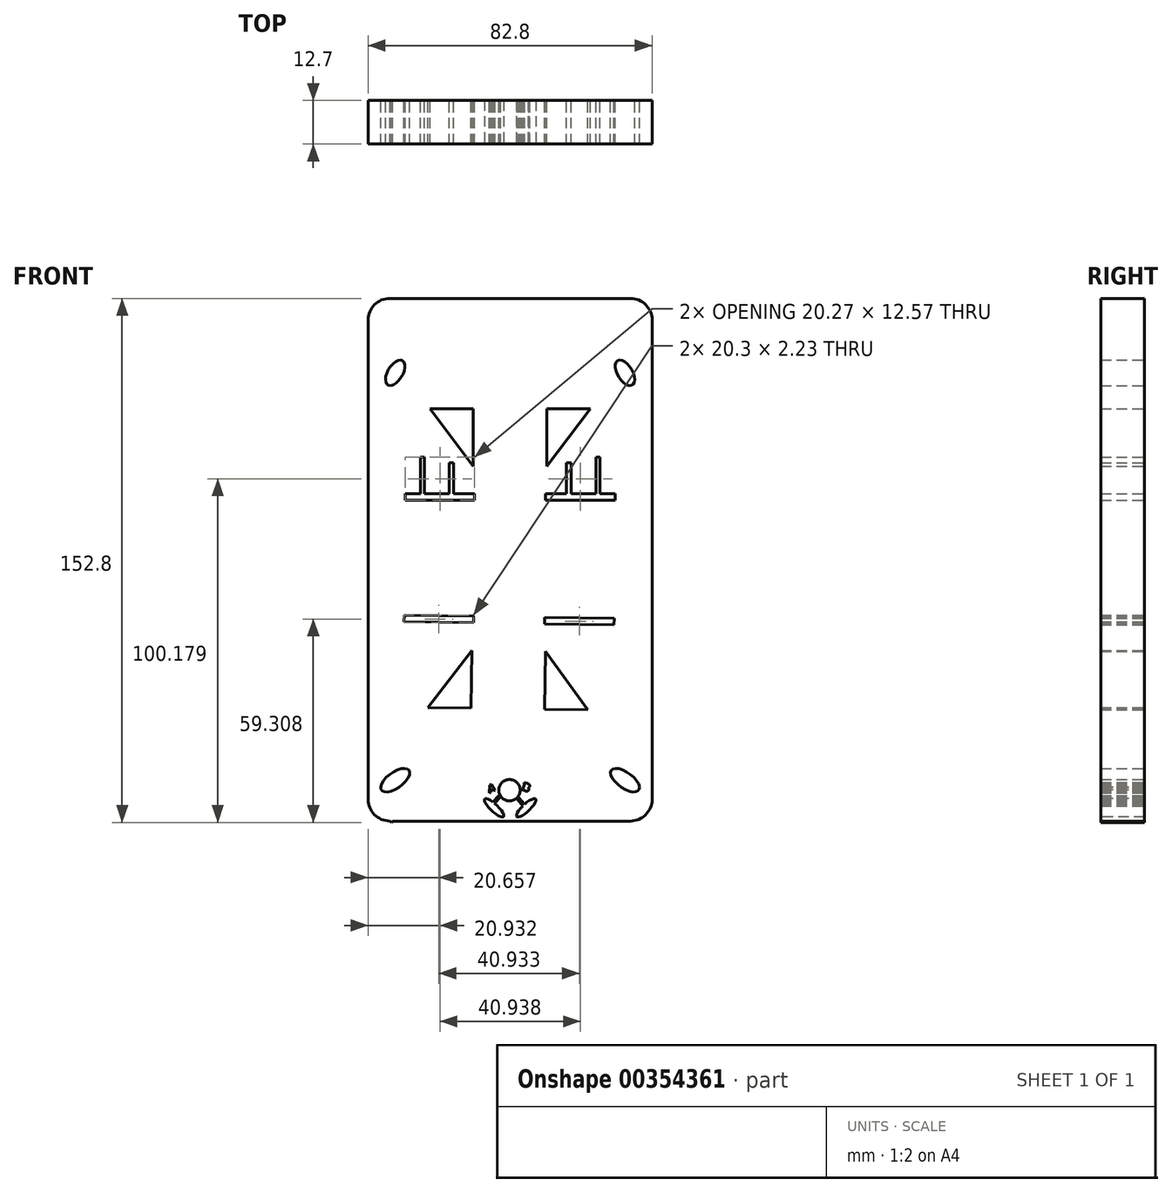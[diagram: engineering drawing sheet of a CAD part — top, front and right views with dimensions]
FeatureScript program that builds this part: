
annotation { "Feature Type Name" : "Feature", "Feature Type Description" : "" }
export const myFeature = defineFeature(function(context is Context, id is Id, definition is map)
    precondition{}
    {
        {
            var Q0;
            Q0=qCreatedBy(makeId("Front.planeOp"),FACE);
            var sketch = newSketch(context, id + "F0", { "sketchPlane" : qUnion([Q0])});
            skLineSegment(sketch, "E0.bottom", {"start": v(-34.85, 75.56) * mm, "end": v(35.25, 75.56) * mm});
            skLineSegment(sketch, "E0.top", {"start": v(-34.85, -76.84) * mm, "end": v(35.25, -76.84) * mm});
            skLineSegment(sketch, "E0.left", {"start": v(-41.2, 69.21) * mm, "end": v(-41.2, -70.49) * mm});
            skLineSegment(sketch, "E0.right", {"start": v(41.6, 69.21) * mm, "end": v(41.6, -70.49) * mm});
            skPoint(sketch, "E1.visualSharp", {"position": v(-41.2, 75.56) * mm});
            skArc(sketch, "E1.filletArc", {"start": v(-34.85, 75.56) * mm, "mid": v(-39.34, 73.7) * mm, "end": v(-41.2, 69.21) * mm});
            skPoint(sketch, "E2.visualSharp", {"position": v(41.6, 75.56) * mm});
            skArc(sketch, "E2.filletArc", {"start": v(41.6, 69.21) * mm, "mid": v(39.74, 73.7) * mm, "end": v(35.25, 75.56) * mm});
            skPoint(sketch, "E3.visualSharp", {"position": v(-41.2, -76.84) * mm});
            skArc(sketch, "E3.filletArc", {"start": v(-41.2, -70.49) * mm, "mid": v(-39.34, -74.98) * mm, "end": v(-34.85, -76.84) * mm});
            skPoint(sketch, "E4.visualSharp", {"position": v(41.6, -76.84) * mm});
            skArc(sketch, "E4.filletArc", {"start": v(35.25, -76.84) * mm, "mid": v(39.74, -74.98) * mm, "end": v(41.6, -70.49) * mm});
            skEllipse(sketch, "E5", {"center": v(-33.29, 53.84) * mm, "majorRadius": 4.13 * mm, "minorRadius": 2.18 * mm, "majorAxis": v(0.52, 0.85)});
            skEllipse(sketch, "E6", {"center": v(-33.29, -64.92) * mm, "majorRadius": 4.95 * mm, "minorRadius": 2.3 * mm, "majorAxis": v(0.81, 0.58)});
            skEllipse(sketch, "E7.MirrorC", {"center": v(33.69, -64.92) * mm, "majorRadius": 4.95 * mm, "minorRadius": 2.3 * mm, "majorAxis": v(-0.81, 0.58)});
            skEllipse(sketch, "E8.MirrorC", {"center": v(33.69, 53.84) * mm, "majorRadius": 4.13 * mm, "minorRadius": 2.18 * mm, "majorAxis": v(-0.52, 0.85)});
            skLineSegment(sketch, "E9", {"start": v(-23.14, 43.43) * mm, "end": v(-10.51, 43.43) * mm});
            skLineSegment(sketch, "E10", {"start": v(-10.51, 43.43) * mm, "end": v(-10.51, 26.6) * mm});
            skLineSegment(sketch, "E11", {"start": v(-10.51, 26.6) * mm, "end": v(-23.14, 43.43) * mm});
            skLineSegment(sketch, "E12.MirrorCS", {"start": v(10.92, 43.43) * mm, "end": v(10.92, 26.6) * mm});
            skLineSegment(sketch, "E13.MirrorCS", {"start": v(23.54, 43.43) * mm, "end": v(10.92, 43.43) * mm});
            skLineSegment(sketch, "E14.MirrorCS", {"start": v(10.92, 26.6) * mm, "end": v(23.54, 43.43) * mm});
            skLineSegment(sketch, "E15", {"start": v(-41.2, 0) * mm, "end": v(41.6, -0.64) * mm});
            skPoint(sketch, "E15.startSnap0", {"position": v(-41.2, -0.64) * mm});
            skLineSegment(sketch, "E16.MirrorCS", {"start": v(-10.93, -27.07) * mm, "end": v(-23.81, -43.7) * mm});
            skLineSegment(sketch, "E17.MirrorCS", {"start": v(-11.19, -43.9) * mm, "end": v(-10.93, -27.07) * mm});
            skLineSegment(sketch, "E18.MirrorCS", {"start": v(-23.81, -43.7) * mm, "end": v(-11.19, -43.9) * mm});
            skLineSegment(sketch, "E19.MirrorCS", {"start": v(10.24, -44.23) * mm, "end": v(10.5, -27.4) * mm});
            skLineSegment(sketch, "E20.MirrorCS", {"start": v(22.86, -44.42) * mm, "end": v(10.24, -44.23) * mm});
            skLineSegment(sketch, "E21.MirrorCS", {"start": v(10.5, -27.4) * mm, "end": v(22.86, -44.42) * mm});
            skLineSegment(sketch, "E22.bottom", {"start": v(-30.4, 18.57) * mm, "end": v(-10.13, 18.57) * mm});
            skLineSegment(sketch, "E22.top", {"start": v(-30.4, 16.65) * mm, "end": v(-10.13, 16.65) * mm});
            skLineSegment(sketch, "E22.left", {"start": v(-30.4, 18.57) * mm, "end": v(-30.4, 16.65) * mm});
            skLineSegment(sketch, "E22.right", {"start": v(-10.13, 18.57) * mm, "end": v(-10.13, 16.65) * mm});
            skLineSegment(sketch, "E23.MirrorCS", {"start": v(30.8, 16.65) * mm, "end": v(10.53, 16.65) * mm});
            skLineSegment(sketch, "E24.MirrorCS", {"start": v(30.8, 18.57) * mm, "end": v(10.53, 18.57) * mm});
            skLineSegment(sketch, "E25.MirrorCS", {"start": v(10.53, 18.57) * mm, "end": v(10.53, 16.65) * mm});
            skLineSegment(sketch, "E26.MirrorCS", {"start": v(30.8, 18.57) * mm, "end": v(30.8, 16.65) * mm});
            skLineSegment(sketch, "E27.MirrorCS", {"start": v(30.54, -17.76) * mm, "end": v(10.27, -17.45) * mm});
            skLineSegment(sketch, "E28.MirrorCS", {"start": v(30.51, -19.68) * mm, "end": v(30.54, -17.76) * mm});
            skLineSegment(sketch, "E29.MirrorCS", {"start": v(30.51, -19.68) * mm, "end": v(10.24, -19.36) * mm});
            skLineSegment(sketch, "E30.MirrorCS", {"start": v(10.24, -19.36) * mm, "end": v(10.27, -17.45) * mm});
            skLineSegment(sketch, "E31.MirrorCS", {"start": v(-30.7, -18.73) * mm, "end": v(-30.66, -16.82) * mm});
            skLineSegment(sketch, "E32.MirrorCS", {"start": v(-30.7, -18.73) * mm, "end": v(-10.42, -19.04) * mm});
            skLineSegment(sketch, "E33.MirrorCS", {"start": v(-10.42, -19.04) * mm, "end": v(-10.4, -17.13) * mm});
            skLineSegment(sketch, "E34.MirrorCS", {"start": v(-30.66, -16.82) * mm, "end": v(-10.4, -17.13) * mm});
            skLineSegment(sketch, "E35.bottom", {"start": v(-16.23, 18.57) * mm, "end": v(-17.57, 18.57) * mm});
            skLineSegment(sketch, "E35.top", {"start": v(-16.23, 27.6) * mm, "end": v(-17.57, 27.6) * mm});
            skLineSegment(sketch, "E35.left", {"start": v(-16.23, 18.57) * mm, "end": v(-16.23, 27.6) * mm});
            skLineSegment(sketch, "E35.right", {"start": v(-17.57, 18.57) * mm, "end": v(-17.57, 27.6) * mm});
            skLineSegment(sketch, "E36.bottom", {"start": v(-25.98, 18.57) * mm, "end": v(-24.83, 18.57) * mm});
            skLineSegment(sketch, "E36.top", {"start": v(-25.98, 29.22) * mm, "end": v(-24.83, 29.22) * mm});
            skLineSegment(sketch, "E36.left", {"start": v(-25.98, 18.57) * mm, "end": v(-25.98, 29.22) * mm});
            skLineSegment(sketch, "E36.right", {"start": v(-24.83, 18.57) * mm, "end": v(-24.83, 29.22) * mm});
            skLineSegment(sketch, "E37.MirrorCS", {"start": v(16.63, 18.57) * mm, "end": v(16.63, 27.6) * mm});
            skLineSegment(sketch, "E38.MirrorCS", {"start": v(17.97, 18.57) * mm, "end": v(17.97, 27.6) * mm});
            skLineSegment(sketch, "E39.MirrorCS", {"start": v(16.63, 27.6) * mm, "end": v(17.97, 27.6) * mm});
            skLineSegment(sketch, "E40.MirrorCS", {"start": v(25.24, 18.57) * mm, "end": v(25.24, 29.22) * mm});
            skLineSegment(sketch, "E41.MirrorCS", {"start": v(26.38, 18.57) * mm, "end": v(26.38, 29.22) * mm});
            skLineSegment(sketch, "E42.MirrorCS", {"start": v(26.38, 29.22) * mm, "end": v(25.24, 29.22) * mm});
            skEllipse(sketch, "E43", {"center": v(-4.48, -72.98) * mm, "majorRadius": 3.76 * mm, "minorRadius": 1.1 * mm, "majorAxis": v(-0.73, 0.69)});
            skEllipse(sketch, "E44.MirrorC", {"center": v(4.88, -72.98) * mm, "majorRadius": 3.76 * mm, "minorRadius": 1.1 * mm, "majorAxis": v(0.73, 0.69)});
            skCircle(sketch, "E45", {"center": v(0, -67.86) * mm, "radius": 3.12 * mm});
            skLineSegment(sketch, "E46.bottom", {"start": v(2.72, -70.01) * mm, "end": v(4.38, -72) * mm});
            skLineSegment(sketch, "E46.top", {"start": v(2.25, -70.41) * mm, "end": v(3.91, -72.4) * mm});
            skLineSegment(sketch, "E46.left", {"start": v(2.72, -70.01) * mm, "end": v(2.25, -70.41) * mm});
            skLineSegment(sketch, "E46.right", {"start": v(4.38, -72) * mm, "end": v(3.91, -72.4) * mm});
            skLineSegment(sketch, "E47.bottom", {"start": v(-32.71, -75.26) * mm, "end": v(-34.38, -77.24) * mm});
            skLineSegment(sketch, "E47.top", {"start": v(-33.19, -74.86) * mm, "end": v(-34.85, -76.84) * mm});
            skLineSegment(sketch, "E47.left", {"start": v(-32.71, -75.26) * mm, "end": v(-33.19, -74.86) * mm});
            skLineSegment(sketch, "E47.right", {"start": v(-34.38, -77.24) * mm, "end": v(-34.85, -76.84) * mm});
            skLineSegment(sketch, "E48.bottom", {"start": v(-2.62, -69.76) * mm, "end": v(-4.35, -71.69) * mm});
            skLineSegment(sketch, "E48.top", {"start": v(-3.08, -69.35) * mm, "end": v(-4.81, -71.27) * mm});
            skLineSegment(sketch, "E48.left", {"start": v(-2.62, -69.76) * mm, "end": v(-3.08, -69.35) * mm});
            skLineSegment(sketch, "E48.right", {"start": v(-4.35, -71.69) * mm, "end": v(-4.81, -71.27) * mm});
            skText(sketch, "E49", { "text": "A", "fontName": "OpenSans-BoldItalic.ttf"});
            skText(sketch, "E50", { "text": "B", "fontName": "RobotoSlab-Bold.ttf"});
            const initialGuessF0  = {"E49": [-0.00571, -0.06858, 0.9063, 0.42262, 0.0021], "E50": [0.00348, -0.06766, 0.9397, -0.34202, 0.0023]};
            skSetInitialGuess(sketch, initialGuessF0);
            skSolve(sketch);
        }
        {
            var Q0;
            Q0 = qSketchRegion(id + "F0", true);
            extrude(context, id + "F1", {"entities" : qUnion([Q0]), "endBound" : BoundingType.SYMMETRIC, "depth" : 12.7 * mm});
        }
    });
